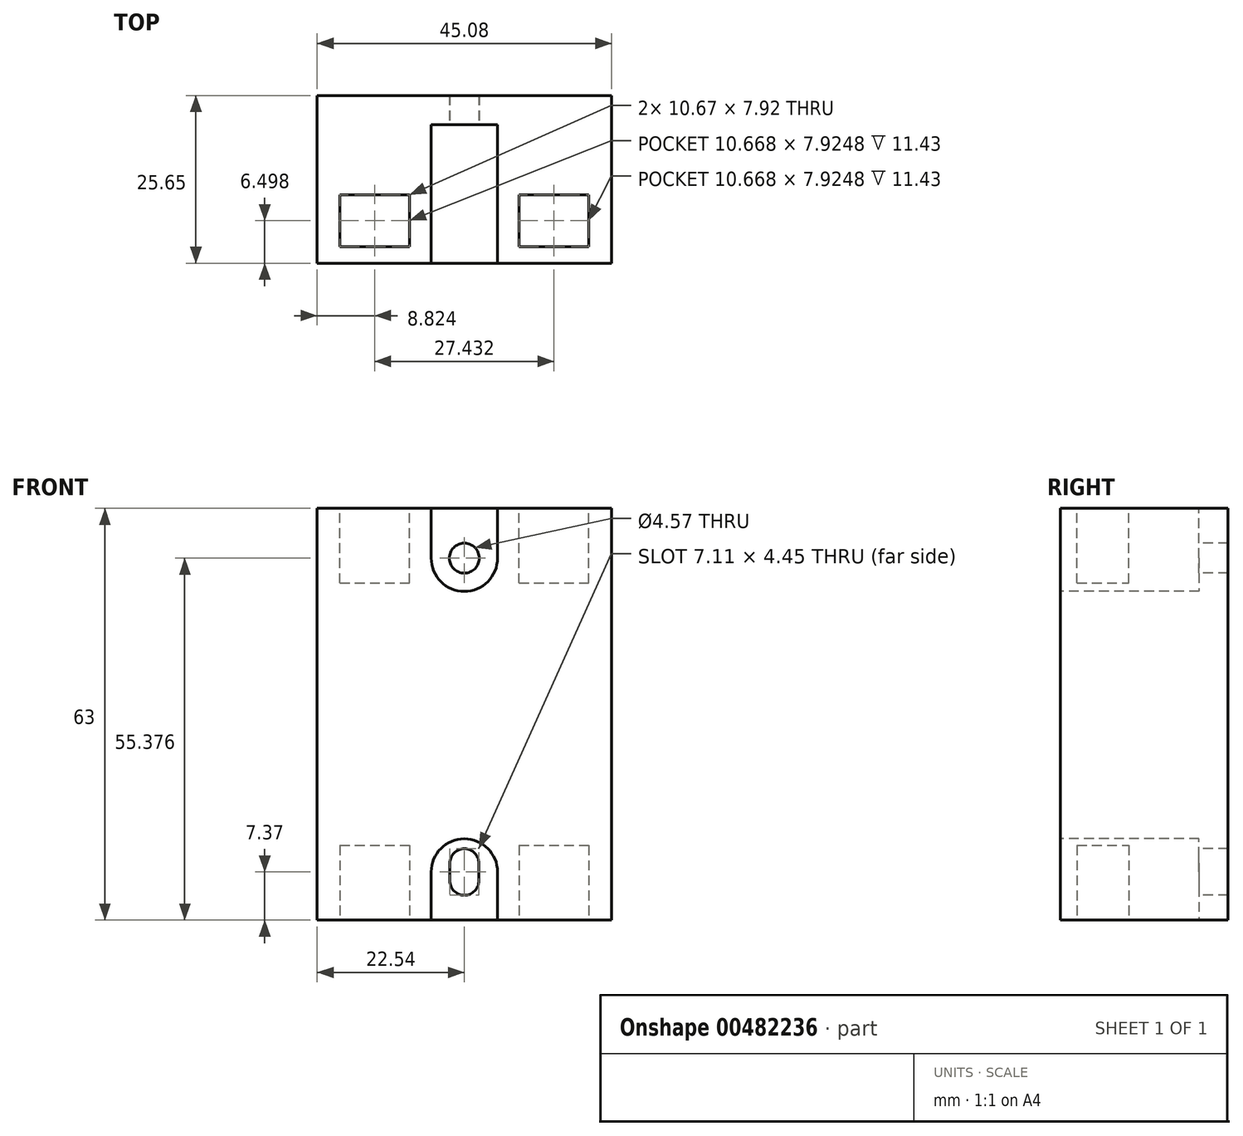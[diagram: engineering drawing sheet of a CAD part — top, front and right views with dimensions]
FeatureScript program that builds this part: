
annotation { "Feature Type Name" : "Feature", "Feature Type Description" : "" }
export const myFeature = defineFeature(function(context is Context, id is Id, definition is map)
    precondition{}
    {
        {
            var Q0;
            Q0=qCreatedBy(makeId("Front.planeOp"),FACE);
            var sketch = newSketch(context, id + "F0", { "sketchPlane" : qUnion([Q0])});
            skLineSegment(sketch, "E0.bottom", {"start": v(22.54, 31.5) * mm, "end": v(-22.54, 31.5) * mm});
            skLineSegment(sketch, "E0.top", {"start": v(22.54, -31.5) * mm, "end": v(-22.54, -31.5) * mm});
            skLineSegment(sketch, "E0.left", {"start": v(22.54, 31.5) * mm, "end": v(22.54, -31.5) * mm});
            skLineSegment(sketch, "E0.right", {"start": v(-22.54, 31.5) * mm, "end": v(-22.54, -31.5) * mm});
            skPoint(sketch, "E0.middle", {"position": v(0, 0) * mm});
            skSolve(sketch);
        }
        {
            var Q0;
            Q0 = qSketchRegion(id + "F0", true);
            extrude(context, id + "F1", {"entities" : qUnion([Q0]), "depth" : 25.65 * mm});
        }
        {
            var Q0;
            Q0=makeQuery(id+"F1.opExtrude","CAP_FACE",FACE,{"disambiguationData":[OSD([sQuery(id+"F0.wireOp",EDGE,"E0.bottom"),sQuery(id+"F0.wireOp",EDGE,"E0.top"),sQuery(id+"F0.wireOp",EDGE,"E0.left"),sQuery(id+"F0.wireOp",EDGE,"E0.right")])],"isStart":false});
            var sketch = newSketch(context, id + "F2", { "sketchPlane" : qUnion([Q0])});
            skCircle(sketch, "E1", {"center": v(0, 23.88) * mm, "radius": 2.29 * mm});
            skArc(sketch, "E2", {"start": v(-2.22, -25.46) * mm, "mid": v(0, -27.69) * mm, "end": v(2.22, -25.46) * mm});
            skArc(sketch, "E3", {"start": v(2.22, -22.8) * mm, "mid": v(0, -20.57) * mm, "end": v(-2.22, -22.8) * mm});
            skLineSegment(sketch, "E4", {"start": v(2.22, -25.46) * mm, "end": v(2.22, -22.8) * mm});
            skLineSegment(sketch, "E5", {"start": v(-2.22, -22.8) * mm, "end": v(-2.22, -25.46) * mm});
            skSolve(sketch);
        }
        {
            var Q0;
            Q0 = qSketchRegion(id + "F2", true);
            extrude(context, id + "F3", {"entities" : qUnion([Q0]), "operationType" : NewBodyOperationType.REMOVE, "oppositeDirection" : true, "depth" : 35.3 * mm});
        }
        {
            var Q0;
            Q0=makeQuery(id+"F1.opExtrude","CAP_FACE",FACE,{"disambiguationData":[OSD([sQuery(id+"F0.wireOp",EDGE,"E0.bottom"),sQuery(id+"F0.wireOp",EDGE,"E0.top"),sQuery(id+"F0.wireOp",EDGE,"E0.left"),sQuery(id+"F0.wireOp",EDGE,"E0.right")])],"isStart":false});
            var sketch = newSketch(context, id + "F4", { "sketchPlane" : qUnion([Q0])});
            skArc(sketch, "E6", {"start": v(-5.08, 23.88) * mm, "mid": v(0, 18.8) * mm, "end": v(5.08, 23.88) * mm});
            skLineSegment(sketch, "E7", {"start": v(5.08, 23.88) * mm, "end": v(5.08, 34.95) * mm});
            skLineSegment(sketch, "E8", {"start": v(-5.08, 23.88) * mm, "end": v(-5.08, 34.95) * mm});
            skLineSegment(sketch, "E9", {"start": v(-5.08, 34.95) * mm, "end": v(5.08, 34.95) * mm});
            skArc(sketch, "E10", {"start": v(5.08, -24.13) * mm, "mid": v(0, -19.05) * mm, "end": v(-5.08, -24.13) * mm});
            skPoint(sketch, "E10.centerSnap0", {"position": v(-2.22, -24.13) * mm});
            skLineSegment(sketch, "E11", {"start": v(5.08, -24.13) * mm, "end": v(5.08, -34.45) * mm});
            skLineSegment(sketch, "E12", {"start": v(5.08, -34.45) * mm, "end": v(-5.08, -34.45) * mm});
            skLineSegment(sketch, "E13", {"start": v(-5.08, -34.45) * mm, "end": v(-5.08, -24.13) * mm});
            skSolve(sketch);
        }
        {
            var Q0;
            Q0 = qSketchRegion(id + "F4", true);
            extrude(context, id + "F5", {"entities" : qUnion([Q0]), "operationType" : NewBodyOperationType.REMOVE, "oppositeDirection" : true, "depth" : 21.2 * mm});
        }
        {
            var Q0;
            Q0=makeQuery(id+"F1.opExtrude","SWEPT_FACE",FACE,{"disambiguationData":[OSD([sQuery(id+"F0.wireOp",EDGE,"E0.top")])]});
            var sketch = newSketch(context, id + "F6", { "sketchPlane" : qUnion([Q0])});
            skLineSegment(sketch, "E14.bottom", {"start": v(-19.05, 23.11) * mm, "end": v(-8.38, 23.11) * mm});
            skLineSegment(sketch, "E14.top", {"start": v(-19.05, 15.19) * mm, "end": v(-8.38, 15.19) * mm});
            skLineSegment(sketch, "E14.left", {"start": v(-19.05, 23.11) * mm, "end": v(-19.05, 15.19) * mm});
            skLineSegment(sketch, "E14.right", {"start": v(-8.38, 23.11) * mm, "end": v(-8.38, 15.19) * mm});
            skLineSegment(sketch, "E15.bottom", {"start": v(8.38, 23.11) * mm, "end": v(19.05, 23.11) * mm});
            skLineSegment(sketch, "E15.top", {"start": v(8.38, 15.19) * mm, "end": v(19.05, 15.19) * mm});
            skLineSegment(sketch, "E15.left", {"start": v(8.38, 23.11) * mm, "end": v(8.38, 15.19) * mm});
            skLineSegment(sketch, "E15.right", {"start": v(19.05, 23.11) * mm, "end": v(19.05, 15.19) * mm});
            skLineSegment(sketch, "E16", {"start": v(-22.54, 19.03) * mm, "end": v(-19.05, 19.03) * mm, "construction": true});
            skLineSegment(sketch, "E17", {"start": v(19.05, 19.03) * mm, "end": v(22.54, 19.03) * mm, "construction": true});
            skSolve(sketch);
        }
        {
            var Q0;
            Q0 = qSketchRegion(id + "F6", true);
            extrude(context, id + "F7", {"entities" : qUnion([Q0]), "operationType" : NewBodyOperationType.REMOVE, "oppositeDirection" : true, "depth" : 11.43 * mm});
        }
        {
            var Q0;
            Q0=makeQuery(id+"F1.opExtrude","SWEPT_FACE",FACE,{"disambiguationData":[OSD([sQuery(id+"F0.wireOp",EDGE,"E0.bottom")])]});
            var sketch = newSketch(context, id + "F8", { "sketchPlane" : qUnion([Q0])});
            skLineSegment(sketch, "E18.0", {"start": v(8.38, -15.19) * mm, "end": v(19.05, -15.19) * mm});
            skLineSegment(sketch, "E18.1", {"start": v(8.38, -23.11) * mm, "end": v(8.38, -15.19) * mm});
            skLineSegment(sketch, "E18.2", {"start": v(8.38, -23.11) * mm, "end": v(19.05, -23.11) * mm});
            skLineSegment(sketch, "E18.3", {"start": v(19.05, -23.11) * mm, "end": v(19.05, -15.19) * mm});
            skLineSegment(sketch, "E19.0", {"start": v(-8.38, -23.11) * mm, "end": v(-8.38, -15.19) * mm});
            skLineSegment(sketch, "E19.1", {"start": v(-19.05, -23.11) * mm, "end": v(-8.38, -23.11) * mm});
            skLineSegment(sketch, "E19.2", {"start": v(-19.05, -23.11) * mm, "end": v(-19.05, -15.19) * mm});
            skLineSegment(sketch, "E19.3", {"start": v(-19.05, -15.19) * mm, "end": v(-8.38, -15.19) * mm});
            skSolve(sketch);
        }
        {
            var Q0;
            Q0 = qSketchRegion(id + "F8", true);
            extrude(context, id + "F9", {"entities" : qUnion([Q0]), "operationType" : NewBodyOperationType.REMOVE, "oppositeDirection" : true, "depth" : 11.43 * mm});
        }
    });
